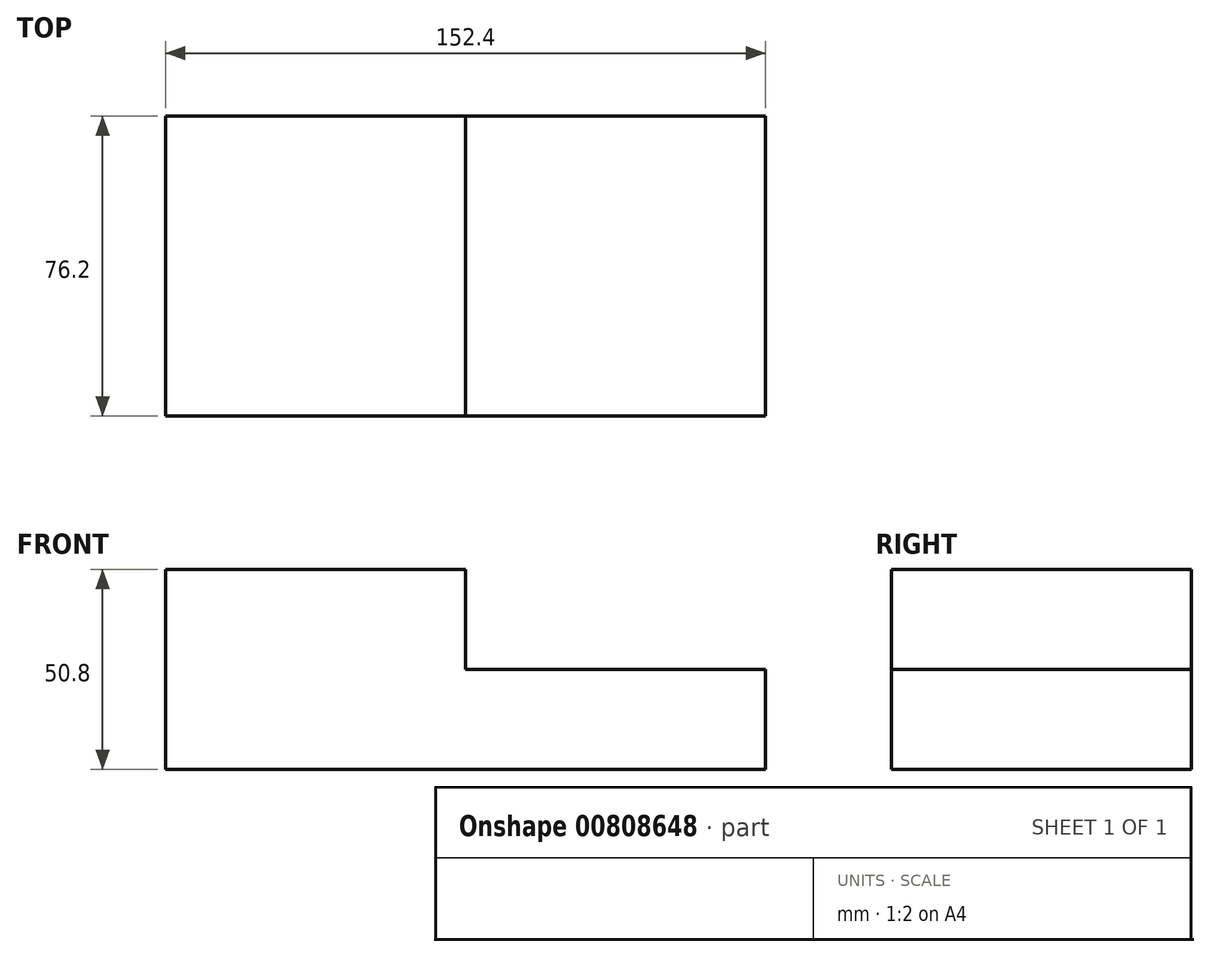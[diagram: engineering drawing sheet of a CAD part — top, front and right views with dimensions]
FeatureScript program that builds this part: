
annotation { "Feature Type Name" : "Feature", "Feature Type Description" : "" }
export const myFeature = defineFeature(function(context is Context, id is Id, definition is map)
    precondition{}
    {
        {
            var Q0;
            Q0=qCreatedBy(makeId("Front.planeOp"),FACE);
            var sketch = newSketch(context, id + "F0", { "sketchPlane" : qUnion([Q0])});
            skLineSegment(sketch, "E0", {"start": v(-76.18, 0) * mm, "end": v(76.22, 0) * mm});
            skLineSegment(sketch, "E1", {"start": v(-76.18, 0) * mm, "end": v(-76.18, 50.8) * mm});
            skLineSegment(sketch, "E2", {"start": v(-76.18, 50.8) * mm, "end": v(0.02, 50.8) * mm});
            skLineSegment(sketch, "E3", {"start": v(0.02, 50.8) * mm, "end": v(0.02, 25.4) * mm});
            skLineSegment(sketch, "E4", {"start": v(0.02, 25.4) * mm, "end": v(76.22, 25.4) * mm});
            skLineSegment(sketch, "E5", {"start": v(76.22, 25.4) * mm, "end": v(76.22, 0) * mm});
            skSolve(sketch);
        }
        {
            var Q0;
            Q0=makeQuery(id+"F0.imprint","IMPRINT",FACE,{"disambiguationData":[TD([[makeQuery(id+"F0.imprint","IMPRINT",EDGE,{"derivedFrom":sQuery(id+"F0.wireOp",EDGE,"E0")}),1.0]])]});
            extrude(context, id + "F1", {"entities" : qUnion([Q0]), "depth" : 76.2 * mm, "offsetDistance" : 25.4 * mm});
        }
    });
